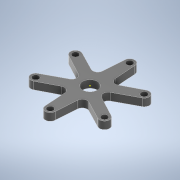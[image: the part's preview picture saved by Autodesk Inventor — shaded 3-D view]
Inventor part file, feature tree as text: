
AUTODESK INVENTOR PART (.ipt)
format: ipt  version: 2021 (Build 250183000, 183)  size: 180,736 bytes
history: native  units: mm
features: sketch x4, hole x2, other x1, extrude x1
ambient origin geometry x8: Origin, YZ Plane, XZ Plane, XY Plane, X Axis, Y Axis, Z Axis, Center Point
bodies: Body1 (feature_tree)
feature tree (8):
  other  "Sólido1"
  extrude  "Extrusión1"  Depth=6.0mm
  hole  "Agujero1"  [1 undecoded]
  hole  "Agujero2"  [1 undecoded]
  sketch  "Boceto4"  dims[d25=2.5mm d26=2.5mm d27=2.5mm d28=2.5mm d29=2.5mm d30=6.0mm d31=4.0mm d32=2.0mm d33=90.0deg d34=8.0mm d35=20.594885mm d36=2.5mm d37=2.5mm d38=6.0mm d39=4.0mm d40=2.0mm d41=90.0deg d42=8.0mm d43=20.594885mm]
  sketch  "Boceto1"  dims[d15=60.0mm d17=360.0deg d19=6.0mm]
  sketch  "Boceto2"  dims[d20=2.0mm d21=3.0mm d22=0.0mm]
  sketch  "Boceto3"  dims[d23=2.5mm d24=2.5mm]
note: 2 required parameter values undecoded (feature->parameter linkage not recoverable at this tier; creation-order binding heuristic only, values carry confidence <= 0.55)
